# Revit family: Скамейка кованая «Вояж»
name_source: partatom
category: Мебель
revit_build: Autodesk Revit 2017 (Build: 20160225_1515(x64)
units: mm (PartAtom-declared; Revit-internal decimal feet)

## family parameters
Всегда вертикально = Да
Заголовок OmniClass = General Furniture and Specialties
На основе рабочей плоскости = Нет
Номер OmniClass = 23.40.20.00
Общий = Нет
При загрузке вырезать с полостями = Нет
Точка расчета площади = Нет

## types (6) — shared parameters
ADSK_Код изделия = 6781
ADSK_Материал доски = <По категории>
ADSK_Материал опоры = <По категории>
ADSK_Материал фурнитуры = <По категории>
ADSK_Размер_Высота = 860 мм
ADSK_Размер_Высота сидения = 430 мм
ADSK_Размер_Высота спинки = 430 мм
ADSK_Размер_Ширина = 720 мм
ADSK_Размер_Ширина сидения = 370 мм
URL = https://hobbyka.ru
Изготовитель = Хоббика

## per-type parameters (varying)
| type | ADSK_Размер_Длина | Длдина доски | Стоимость | Центральная опора |
| Скамейка кованая «Вояж» 1,2м | 1200 мм | 1180 мм | 8489 $ | Нет |
| Скамейка кованая «Вояж» 1,5м | 1500 мм | 1480 мм | 9041 $ | Нет |
| Скамейка кованая «Вояж» 1,8м | 1800 мм | 1780 мм | 9702 $ | Нет |
| Скамейка кованая «Вояж» 2,0м | 2000 мм | 1980 мм | 14553 $ | Да |
| Скамейка кованая «Вояж» 3,0м | 3000 мм | 2980 мм | 14553 $ | Да |
| Скамейка кованая «Вояж» Кресло | 600 мм | 580 мм | 7938 $ | Нет |

note: column(s) folded — value = type name in every type: ADSK_Наименование
